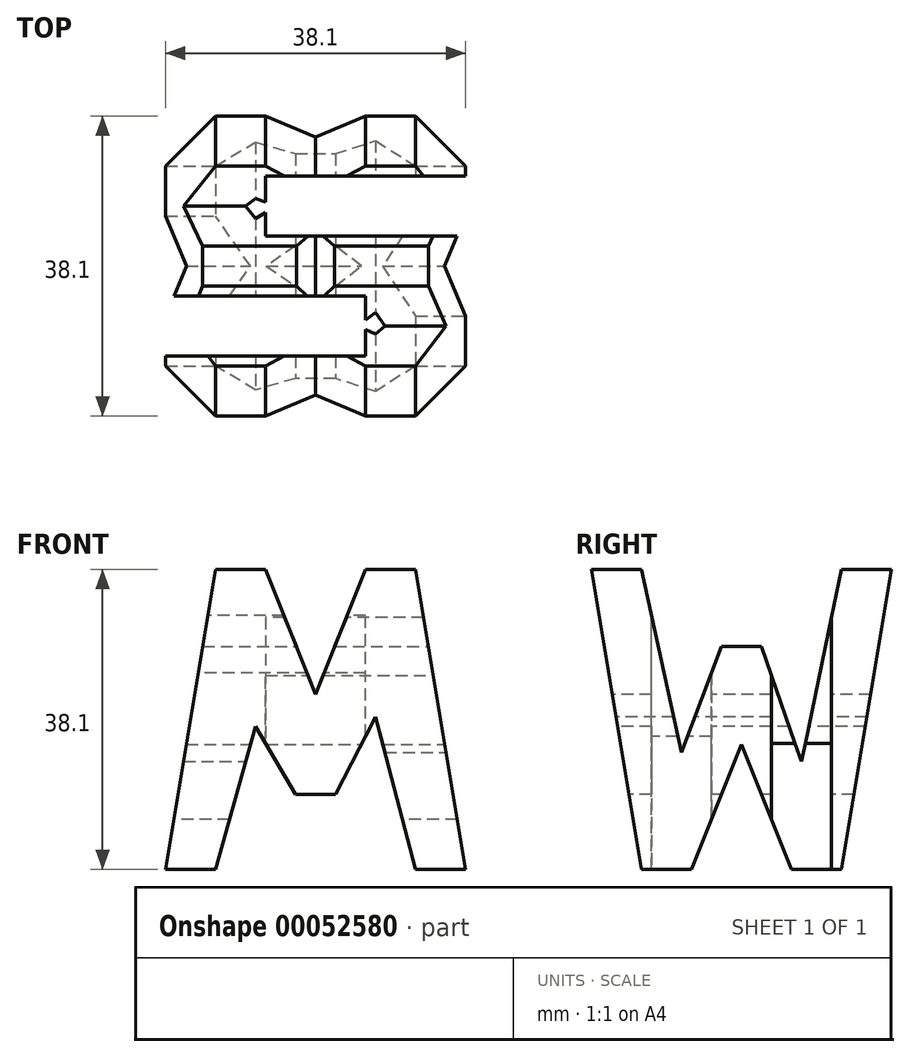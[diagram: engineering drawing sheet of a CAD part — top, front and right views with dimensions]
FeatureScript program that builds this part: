
annotation { "Feature Type Name" : "Feature", "Feature Type Description" : "" }
export const myFeature = defineFeature(function(context is Context, id is Id, definition is map)
    precondition{}
    {
        {
            var Q0;
            Q0=qCreatedBy(makeId("Front.planeOp"),FACE);
            var sketch = newSketch(context, id + "F0", { "sketchPlane" : qUnion([Q0])});
            skLineSegment(sketch, "E0", {"start": v(0, 0) * mm, "end": v(38.1, 0) * mm});
            skLineSegment(sketch, "E1", {"start": v(38.1, 0) * mm, "end": v(38.1, 38.1) * mm});
            skLineSegment(sketch, "E2", {"start": v(0, 0) * mm, "end": v(0, 38.1) * mm});
            skLineSegment(sketch, "E3", {"start": v(0, 38.1) * mm, "end": v(38.1, 38.1) * mm});
            skSolve(sketch);
        }
        {
            var Q0;
            Q0=makeQuery(id+"F0.imprint","IMPRINT",FACE,{"disambiguationData":[TD([[makeQuery(id+"F0.imprint","IMPRINT",EDGE,{"derivedFrom":sQuery(id+"F0.wireOp",EDGE,"E0")}),1.0]])]});
            extrude(context, id + "F1", {"entities" : qUnion([Q0]), "depth" : 38.1 * mm});
        }
        {
            var Q0;
            Q0=qCreatedBy(makeId("Front.planeOp"),FACE);
            cPlane(context, id + "F2", {"entities" : qUnion([Q0]), "cplaneType" : CPlaneType.OFFSET, "offset" : 38.1 * mm, "width" : 152.4 * mm, "height" : 152.4 * mm});
        }
        {
            var Q0;
            Q0=qCreatedBy(makeId("Right.planeOp"),FACE);
            cPlane(context, id + "F3", {"entities" : qUnion([Q0]), "cplaneType" : CPlaneType.OFFSET, "offset" : 38.1 * mm, "width" : 152.4 * mm, "height" : 152.4 * mm});
        }
        {
            var Q0;
            Q0=qCreatedBy(makeId("Top.planeOp"),FACE);
            cPlane(context, id + "F4", {"entities" : qUnion([Q0]), "cplaneType" : CPlaneType.OFFSET, "offset" : 38.1 * mm, "width" : 152.4 * mm, "height" : 152.4 * mm});
        }
        {
            var Q0;
            Q0=qCreatedBy(id+"F3.planeOp",FACE);
            var sketch = newSketch(context, id + "F5", { "sketchPlane" : qUnion([Q0])});
            skLineSegment(sketch, "E4", {"start": v(0, 0) * mm, "end": v(0, 38.1) * mm});
            skLineSegment(sketch, "E5", {"start": v(0, 38.1) * mm, "end": v(-38.1, 38.1) * mm});
            skLineSegment(sketch, "E6", {"start": v(-38.1, 38.1) * mm, "end": v(-38.1, 0) * mm});
            skLineSegment(sketch, "E7", {"start": v(-38.1, 0) * mm, "end": v(0, 0) * mm});
            skLineSegment(sketch, "E8", {"start": v(-38.1, 38.1) * mm, "end": v(-31.75, 0) * mm});
            skLineSegment(sketch, "E9", {"start": v(-25.4, 0) * mm, "end": v(-19.05, 15.88) * mm});
            skLineSegment(sketch, "E10", {"start": v(-19.05, 15.88) * mm, "end": v(-12.7, 0) * mm});
            skLineSegment(sketch, "E11", {"start": v(-6.35, 0) * mm, "end": v(0, 38.1) * mm});
            skLineSegment(sketch, "E12", {"start": v(-6.35, 38.1) * mm, "end": v(-11.43, 13.71) * mm});
            skLineSegment(sketch, "E13", {"start": v(-11.43, 13.71) * mm, "end": v(-16.5, 28.32) * mm});
            skLineSegment(sketch, "E14", {"start": v(-16.5, 28.32) * mm, "end": v(-21.59, 28.32) * mm});
            skLineSegment(sketch, "E15", {"start": v(-26.67, 14.84) * mm, "end": v(-31.75, 38.1) * mm});
            skLineSegment(sketch, "E16", {"start": v(-26.67, 14.84) * mm, "end": v(-21.59, 28.32) * mm});
            skSolve(sketch);
        }
        {
            var Q0;
            {var subQ0=sQuery(id+"F5.wireOp",EDGE,"E6");Q0=makeQuery(id+"F5.imprint","IMPRINT",FACE,{"disambiguationData":[TD([[makeQuery(id+"F5.imprint","IMPRINT",EDGE,{"derivedFrom":subQ0}),1.0]])]});}
            var Q1;
            {var subQ0=sQuery(id+"F5.wireOp",EDGE,"E12");Q1=makeQuery(id+"F5.imprint","IMPRINT",FACE,{"disambiguationData":[TD([[makeQuery(id+"F5.imprint","IMPRINT",EDGE,{"derivedFrom":subQ0}),-1.0]])]});}
            var Q2;
            {var subQ0=sQuery(id+"F5.wireOp",EDGE,"E9");Q2=makeQuery(id+"F5.imprint","IMPRINT",FACE,{"disambiguationData":[TD([[makeQuery(id+"F5.imprint","IMPRINT",EDGE,{"derivedFrom":subQ0}),-1.0]])]});}
            var Q3;
            {var subQ0=sQuery(id+"F5.wireOp",EDGE,"E4");Q3=makeQuery(id+"F5.imprint","IMPRINT",FACE,{"disambiguationData":[TD([[makeQuery(id+"F5.imprint","IMPRINT",EDGE,{"derivedFrom":subQ0}),1.0]])]});}
            extrude(context, id + "F6", {"entities" : qUnion([Q0, Q1, Q2, Q3]), "operationType" : NewBodyOperationType.REMOVE, "oppositeDirection" : true, "depth" : 38.1 * mm});
        }
        {
            var Q0;
            Q0=qCreatedBy(id+"F2.planeOp",FACE);
            var sketch = newSketch(context, id + "F7", { "sketchPlane" : qUnion([Q0])});
            skLineSegment(sketch, "E17", {"start": v(0, 0) * mm, "end": v(0, 38.1) * mm});
            skLineSegment(sketch, "E18", {"start": v(0, 38.1) * mm, "end": v(38.1, 38.1) * mm});
            skLineSegment(sketch, "E19", {"start": v(38.1, 38.1) * mm, "end": v(38.1, 0) * mm});
            skLineSegment(sketch, "E20", {"start": v(38.1, 0) * mm, "end": v(0, 0) * mm});
            skLineSegment(sketch, "E21", {"start": v(0, 0) * mm, "end": v(6.35, 38.1) * mm});
            skLineSegment(sketch, "E22", {"start": v(12.7, 38.1) * mm, "end": v(19.05, 22.23) * mm});
            skLineSegment(sketch, "E23", {"start": v(19.05, 22.23) * mm, "end": v(25.4, 38.1) * mm});
            skLineSegment(sketch, "E24", {"start": v(31.75, 38.1) * mm, "end": v(38.1, 0) * mm});
            skLineSegment(sketch, "E25", {"start": v(31.75, 0) * mm, "end": v(26.67, 19.36) * mm});
            skLineSegment(sketch, "E26", {"start": v(26.67, 19.36) * mm, "end": v(21.59, 9.52) * mm});
            skLineSegment(sketch, "E27", {"start": v(21.59, 9.53) * mm, "end": v(16.51, 9.53) * mm});
            skLineSegment(sketch, "E28", {"start": v(16.5, 9.53) * mm, "end": v(11.43, 18.2) * mm});
            skLineSegment(sketch, "E29", {"start": v(11.43, 18.2) * mm, "end": v(6.35, 0) * mm});
            skSolve(sketch);
        }
        {
            var Q0;
            {var subQ0=sQuery(id+"F7.wireOp",EDGE,"E17");Q0=makeQuery(id+"F7.imprint","IMPRINT",FACE,{"disambiguationData":[TD([[makeQuery(id+"F7.imprint","IMPRINT",EDGE,{"derivedFrom":subQ0}),-1.0]])]});}
            var Q1;
            {var subQ0=sQuery(id+"F7.wireOp",EDGE,"E22");Q1=makeQuery(id+"F7.imprint","IMPRINT",FACE,{"disambiguationData":[TD([[makeQuery(id+"F7.imprint","IMPRINT",EDGE,{"derivedFrom":subQ0}),1.0]])]});}
            var Q2;
            {var subQ0=sQuery(id+"F7.wireOp",EDGE,"E25");Q2=makeQuery(id+"F7.imprint","IMPRINT",FACE,{"disambiguationData":[TD([[makeQuery(id+"F7.imprint","IMPRINT",EDGE,{"derivedFrom":subQ0}),1.0]])]});}
            var Q3;
            {var subQ0=sQuery(id+"F7.wireOp",EDGE,"E19");Q3=makeQuery(id+"F7.imprint","IMPRINT",FACE,{"disambiguationData":[TD([[makeQuery(id+"F7.imprint","IMPRINT",EDGE,{"derivedFrom":subQ0}),-1.0]])]});}
            extrude(context, id + "F8", {"entities" : qUnion([Q0, Q1, Q2, Q3]), "operationType" : NewBodyOperationType.REMOVE, "oppositeDirection" : true, "depth" : 38.1 * mm});
        }
        {
            var Q0;
            Q0=qCreatedBy(id+"F4.planeOp",FACE);
            var sketch = newSketch(context, id + "F9", { "sketchPlane" : qUnion([Q0])});
            skLineSegment(sketch, "E30", {"start": v(0, 0) * mm, "end": v(38.1, 0) * mm});
            skLineSegment(sketch, "E31", {"start": v(38.1, 0) * mm, "end": v(38.1, -38.1) * mm});
            skLineSegment(sketch, "E32", {"start": v(0, 0) * mm, "end": v(0, -38.1) * mm});
            skLineSegment(sketch, "E33", {"start": v(0, -38.1) * mm, "end": v(38.1, -38.1) * mm});
            skLineSegment(sketch, "E34", {"start": v(38.1, -7.62) * mm, "end": v(12.7, -7.62) * mm});
            skLineSegment(sketch, "E35", {"start": v(12.7, -7.62) * mm, "end": v(12.7, -15.24) * mm});
            skLineSegment(sketch, "E36", {"start": v(12.7, -15.24) * mm, "end": v(38.1, -15.24) * mm});
            skLineSegment(sketch, "E37", {"start": v(0, -22.86) * mm, "end": v(25.4, -22.86) * mm});
            skLineSegment(sketch, "E38", {"start": v(25.4, -22.86) * mm, "end": v(25.4, -30.48) * mm});
            skLineSegment(sketch, "E39", {"start": v(25.4, -30.48) * mm, "end": v(0, -30.48) * mm});
            skSolve(sketch);
        }
        {
            var Q0;
            {var subQ0=sQuery(id+"F9.wireOp",EDGE,"E34");Q0=makeQuery(id+"F9.imprint","IMPRINT",FACE,{"disambiguationData":[TD([[makeQuery(id+"F9.imprint","IMPRINT",EDGE,{"derivedFrom":subQ0}),1.0]])]});}
            var Q1;
            {var subQ0=sQuery(id+"F9.wireOp",EDGE,"E37");Q1=makeQuery(id+"F9.imprint","IMPRINT",FACE,{"disambiguationData":[TD([[makeQuery(id+"F9.imprint","IMPRINT",EDGE,{"derivedFrom":subQ0}),-1.0]])]});}
            extrude(context, id + "F10", {"entities" : qUnion([Q0, Q1]), "operationType" : NewBodyOperationType.REMOVE, "oppositeDirection" : true, "depth" : 38.1 * mm});
        }
    });
